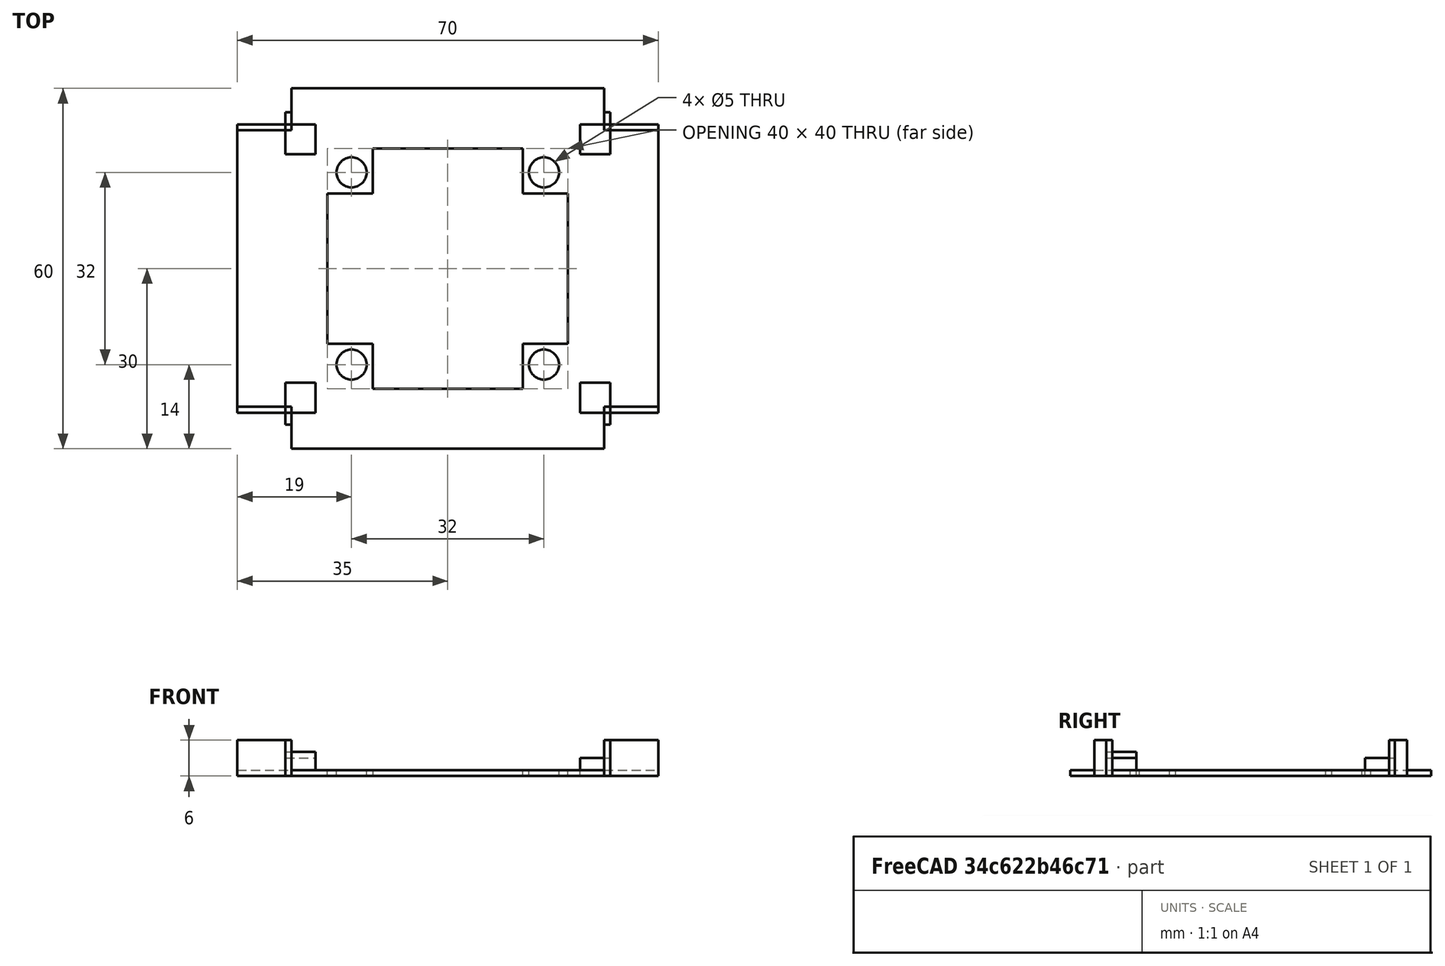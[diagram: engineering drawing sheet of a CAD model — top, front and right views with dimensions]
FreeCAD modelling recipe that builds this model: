
FCSTD DOCUMENT  (FreeCAD 0.18.3R)
Label: M11SDVFan 
License: All rights reserved
LicenseURL: http://en.wikipedia.org/wiki/All_rights_reserved
objects: Part::Box×19, Part::Compound×5, Part::Cut×4, Part::Cylinder×4
note: 32 computed .brp shape members not serialized (recipe doc carries the construction recipe); baked Part::Feature solids carry a one-line shape summary decoded from their .brp

FEATURE [Part::Box] Box  label="WholeCover"
  AttacherType = Attacher::AttachEngine3D
  Height = 1
  Length = 70
  Width = 60
FEATURE [Part::Box] Box002  label="Corner-BL"
  AttacherType = Attacher::AttachEngine3D
  Height = 1
  Length = 9
  Width = 7
FEATURE [Part::Box] Box003  label="Corner-TR"
  AttacherType = Attacher::AttachEngine3D
  Height = 1
  Length = 9
  Placement = pos=(61,53,0) rot=(0,0,1;0rad)
  Width = 7
FEATURE [Part::Box] Box004  label="Corner-BR"
  AttacherType = Attacher::AttachEngine3D
  Height = 1
  Length = 9
  Placement = pos=(61,0,0) rot=(0,0,1;0rad)
  Width = 7
FEATURE [Part::Box] Box005  label="Corner-TL"
  AttacherType = Attacher::AttachEngine3D
  Height = 1
  Length = 9
  Placement = pos=(0,53,0) rot=(0,0,1;0rad)
  Width = 7
FEATURE [Part::Compound] Compound  label="Corners"
  Links = -> [Box004,Box005,Box002,Box003]
FEATURE [Part::Cut] Cut
  Base = -> Box
  Tool = -> Compound
FEATURE [Part::Cylinder] Cylinder  label="Hole-BR"
  Angle = 360
  AttacherType = Attacher::AttachEngine3D
  Height = 1
  Placement = pos=(32,-1,0) rot=(0,0,1;0rad)
  Radius = 2.5
FEATURE [Part::Cylinder] Cylinder001  label="Hole-TL"
  Angle = 360
  AttacherType = Attacher::AttachEngine3D
  Height = 1
  Placement = pos=(0,31,0) rot=(0,0,1;0rad)
  Radius = 2.5
FEATURE [Part::Cylinder] Cylinder002  label="Hole-TR"
  Angle = 360
  AttacherType = Attacher::AttachEngine3D
  Height = 1
  Placement = pos=(32,31,0) rot=(0,0,1;0rad)
  Radius = 2.5
FEATURE [Part::Cylinder] Cylinder003  label="Hole-BL"
  Angle = 360
  AttacherType = Attacher::AttachEngine3D
  Height = 1
  Placement = pos=(0,-1,0) rot=(0,0,1;0rad)
  Radius = 2.5
FEATURE [Part::Compound] Compound001  label="Holes"
  Links = -> [Cylinder003,Cylinder002,Cylinder001,Cylinder]
  Placement = pos=(19,15,0) rot=(0,0,1;0rad)
FEATURE [Part::Cut] Cut001
  Base = -> Cut
  Tool = -> Compound001
FEATURE [Part::Box] Box006  label="Latch-H-TR"
  AttacherType = Attacher::AttachEngine3D
  Height = 6
  Length = 9
  Placement = pos=(61,53,0) rot=(0,0,1;0rad)
  Width = 1
FEATURE [Part::Box] Box007  label="Latch-H-BR"
  AttacherType = Attacher::AttachEngine3D
  Height = 6
  Length = 9
  Placement = pos=(61,6,0) rot=(0,0,1;0rad)
  Width = 1
FEATURE [Part::Box] Box008  label="Latch-H-BL"
  AttacherType = Attacher::AttachEngine3D
  Height = 6
  Length = 9
  Placement = pos=(0,6,0) rot=(0,0,1;0rad)
  Width = 1
FEATURE [Part::Box] Box009  label="Latch-H-TL"
  AttacherType = Attacher::AttachEngine3D
  Height = 6
  Length = 9
  Placement = pos=(0,53,0) rot=(0,0,1;0rad)
  Width = 1
FEATURE [Part::Box] Box010  label="Standoff-TR"
  AttacherType = Attacher::AttachEngine3D
  Height = 3
  Length = 5
  Placement = pos=(57,49,0) rot=(0,0,1;0rad)
  Width = 5
FEATURE [Part::Box] Box011  label="Standoff-BR"
  AttacherType = Attacher::AttachEngine3D
  Height = 3
  Length = 5
  Placement = pos=(57,6,0) rot=(0,0,1;0rad)
  Width = 5
FEATURE [Part::Box] Box012  label="Standoff-TL"
  AttacherType = Attacher::AttachEngine3D
  Height = 3
  Length = 5
  Placement = pos=(8,49,0) rot=(0,0,1;0rad)
  Width = 5
FEATURE [Part::Box] Box013  label="Standoff-BL"
  AttacherType = Attacher::AttachEngine3D
  Height = 3
  Length = 5
  Placement = pos=(8,6,1) rot=(0,0,1;0rad)
  Width = 5
FEATURE [Part::Compound] Compound002  label="Standoffs"
  Links = -> [Box013,Box010,Box011,Box012]
FEATURE [Part::Box] Box014  label="FanCutout-V"
  AttacherType = Attacher::AttachEngine3D
  Height = 1
  Length = 25
  Placement = pos=(22.5,10,0) rot=(0,0,1;0rad)
  Width = 40
FEATURE [Part::Box] Box015  label="FanCutout-H"
  AttacherType = Attacher::AttachEngine3D
  Height = 1
  Length = 40
  Placement = pos=(15,17.5,0) rot=(0,0,1;0rad)
  Width = 25
FEATURE [Part::Box] Box016  label="Latch-V-TL"
  AttacherType = Attacher::AttachEngine3D
  Height = 6
  Length = 1
  Placement = pos=(8,53,0) rot=(0,0,1;0rad)
  Width = 3
FEATURE [Part::Box] Box017  label="Latch-V-TR"
  AttacherType = Attacher::AttachEngine3D
  Height = 6
  Length = 1
  Placement = pos=(61,53,0) rot=(0,0,1;0rad)
  Width = 3
FEATURE [Part::Box] Box018  label="Latch-V-BR"
  AttacherType = Attacher::AttachEngine3D
  Height = 6
  Length = 1
  Placement = pos=(61,4,0) rot=(0,0,1;0rad)
  Width = 3
FEATURE [Part::Box] Box019  label="Latch-V-BL"
  AttacherType = Attacher::AttachEngine3D
  Height = 6
  Length = 1
  Placement = pos=(8,4,0) rot=(0,0,1;0rad)
  Width = 3
FEATURE [Part::Compound] Compound004  label="Latches"
  Links = -> [Box006,Box007,Box008,Box009,Box016,Box017,Box018,Box019]
FEATURE [Part::Compound] Compound003
  Links = -> [Compound002,Cut001,Compound004]
FEATURE [Part::Cut] Cut002
  Base = -> Compound003
  Tool = -> Box015
FEATURE [Part::Cut] Cut003
  Base = -> Cut002
  Tool = -> Box014
